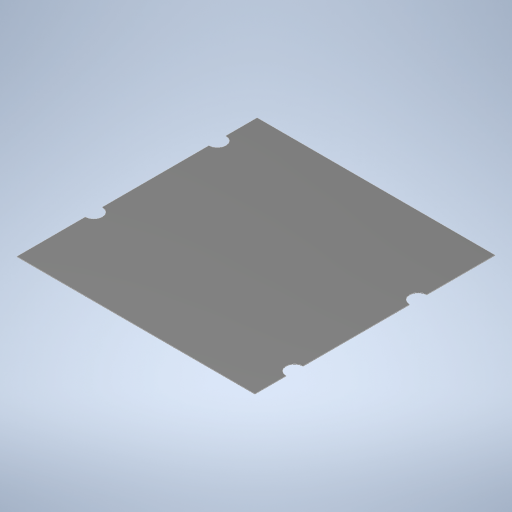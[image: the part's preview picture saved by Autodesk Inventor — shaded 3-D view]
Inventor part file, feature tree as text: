
AUTODESK INVENTOR PART (.ipt)
format: ipt  version: 2023 (Build 270158000, 158)  size: 242,688 bytes
history: native  units: in
note: dims shown in document units (in); Inventor stores cm internally (conversion verified against a paired STEP export)
features: extrude x2, sketch x2
ambient origin geometry x8: Origin, YZ Plane, XZ Plane, XY Plane, X Axis, Y Axis, Z Axis, Center Point
bodies: Solid1 (feature_tree)
feature tree (4):
  extrude  "Extrusion1"  Depth=1.6378in
  extrude  "Extrusion2"  Depth=0.0591in
  sketch  "Sketch1"  dims[d0=1.6535in d1=1.6378in]
  sketch  "Sketch2"  dims[d2=0.0031in d3=0.0in d5=0.0591in d6=0.0031in d7=0.0in d8=0.1181in d9=0.2736in d10=0.0591in d11=0.0591in d12=0.0591in d13=1.1244in d14=0.2736in d15=1.1244in]
